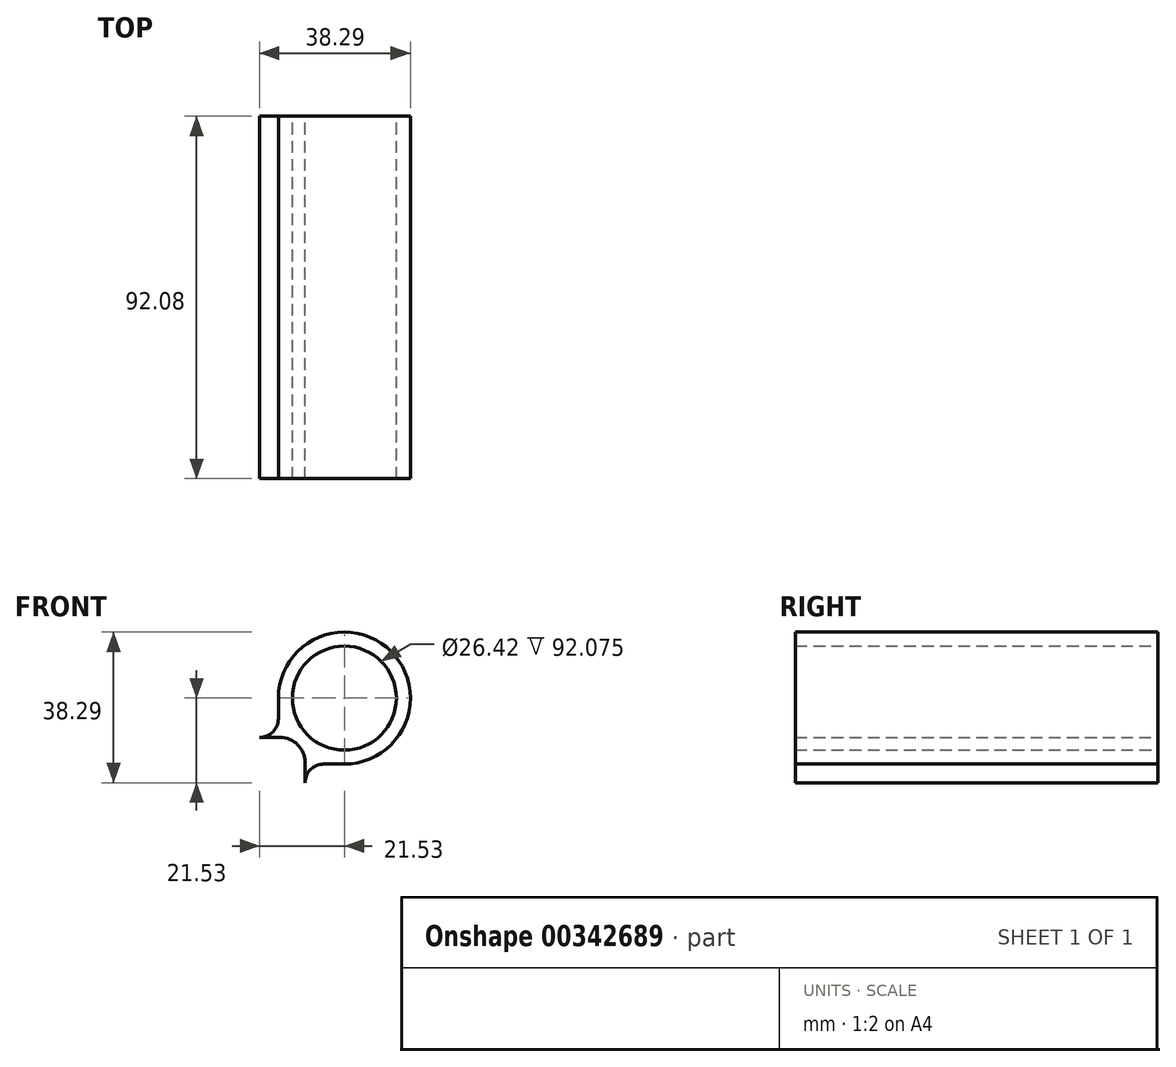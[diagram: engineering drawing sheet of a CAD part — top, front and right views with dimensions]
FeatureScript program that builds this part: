
annotation { "Feature Type Name" : "Feature", "Feature Type Description" : "" }
export const myFeature = defineFeature(function(context is Context, id is Id, definition is map)
    precondition{}
    {
        {
            var Q0;
            Q0=qCreatedBy(makeId("Front.planeOp"),FACE);
            var sketch = newSketch(context, id + "F0", { "sketchPlane" : qUnion([Q0])});
            skArc(sketch, "E0", {"start": v(0, -16.76) * mm, "mid": v(11.85, 11.85) * mm, "end": v(-16.76, 0) * mm});
            skPoint(sketch, "E1.visualSharp", {"position": v(-10, -10) * mm});
            skArc(sketch, "E1.filletArc", {"start": v(-10, -16.34) * mm, "mid": v(-11.85, -11.85) * mm, "end": v(-16.34, -10) * mm});
            skPoint(sketch, "E2.visualSharp", {"position": v(-14.76, -14.76) * mm});
            skLineSegment(sketch, "E3", {"start": v(-11.85, -11.85) * mm, "end": v(-11.85, -11.85) * mm});
            skLineSegment(sketch, "E4", {"start": v(-16.76, 0) * mm, "end": v(-16.76, -5.23) * mm});
            skArc(sketch, "E5.filletArc", {"start": v(-21.53, -10) * mm, "mid": v(-18.16, -8.6) * mm, "end": v(-16.76, -5.23) * mm});
            skArc(sketch, "E6.MirrorCS", {"start": v(-10, -21.53) * mm, "mid": v(-8.6, -18.16) * mm, "end": v(-5.23, -16.76) * mm});
            skLineSegment(sketch, "E7.MirrorCS", {"start": v(0, -16.76) * mm, "end": v(-5.23, -16.76) * mm});
            skLineSegment(sketch, "E8", {"start": v(-16.34, -10) * mm, "end": v(-21.53, -10) * mm});
            skLineSegment(sketch, "E9", {"start": v(-10, -16.34) * mm, "end": v(-10, -21.53) * mm});
            skCircle(sketch, "E10", {"center": v(0, 0) * mm, "radius": 13.2 * mm});
            skSolve(sketch);
        }
        {
            var Q0;
            Q0=makeQuery(id+"F0.imprint","IMPRINT",FACE,{"disambiguationData":[TD([[makeQuery(id+"F0.imprint","IMPRINT",EDGE,{"derivedFrom":sQuery(id+"F0.wireOp",EDGE,"E0")}),1.0]])]});
            extrude(context, id + "F1", {"entities" : qUnion([Q0]), "depth" : 92.07 * mm});
        }
    });
